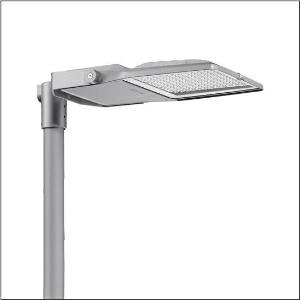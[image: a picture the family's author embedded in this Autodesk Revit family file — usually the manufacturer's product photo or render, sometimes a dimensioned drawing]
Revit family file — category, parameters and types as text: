
# Revit family: floodlight_fl_21_iq_midi___pl64_5xa7782f4e3a_0b41
name_source: partatom
category: Lighting Fixtures
units: mm (PartAtom-declared; Revit-internal decimal feet)

## family parameters
Cut with Voids When Loaded = No
Host = Face
Light Source = No
Part Type = Normal
Room Calculation Point = No
Round Connector Dimension = Use Diameter
Shared = No

## types (1)
- --- (1 x LED, 36050 lm, 270.2 W, 4000K)
    Apparent Load = 270 VA
    CIE Flux Codes = 28 80 98 100 100
    Color Rendering = 70
    Color Temperature = 4000K
    Default Elevation = 1800 mm
    Description = Floodlight FL 21 iQ midi, floodlight, primary light control with lens, of PMMA, primary optical cover: protective disc, of toughened safety glass, transparent, light distribution: PL64, light emission: direct distribution, installation type: surface-mounted, lamps: LED, High Power LED, rated values: 36.050lm | 270,2W | 133,4lm/W (begin service life); end service life: 36.050lm | 286,6W; at 50% lumin. flux: 18.025lm | 117,7W | 153,1lm/W, colour temperature: 4000K, colour rendering: CRI > 70, light colour: 740, light setting 1 begin service life: 100% | 36.050lm | 270,2W | 133,4lm/W | 4.000K, light setting 1 end service life: 286,6W, further light settings possible, control: optimised constant luminous flux control (CLO 2.0), Desk-Remote (wireless, voltage-free reading and setting of iQ features in the workshop via application-optimized NFC function/RFID function), Smart-Wire, Night-Set, Temp-Guard, Auto-Match, Street-Remote, pre-setting: linear dimming characteristic, with terminal, 6-pole, mains connection: 220..240V, AC, 50/60Hz, luminaire housing, of diecast aluminium, powder-coated, SITECO metallic grey (DB 702S), corrosivity category C5 mid according to DIN EN ISO 12944suitable for swimming poolschlorine-resistant, sealing non-destructively replaceable, please order mast flange separately, mast bracket, of steel, galvanised, powder-coated, SITECO metallic grey (DB 702S), protection rating (complete): IP66, insulation class (complete): insulation class II (safety insulation), certification: CE, ENEC, VDE, protection symbol: D, impact resistance: IK08, permissible operating ambient temperature: -40..+40°C, permissible operating ambient temperature for outdoor applications: -40..+50°C, standard: DIN EN 12944, LABS conformity tested according to VDMA 24364:2018-05, packaging unit: 1 piece

Light Distribution: PL64
    Height = 76 mm
    Lamp = 1 x LED
    Lamp Light Flux = 36050 lm
    Lamp Power = 270.2 W
    Lamp count = 1
    Length = 657 mm
    Luminous efficacy = 133 lm/W
    Manufacturer = Siteco
    ModVariant = No
    Model = 5XA7782F4E3A
    Mounting Place = Pole
    Mounting Type = Pole annexe
    Number of Poles = 1
    OnlyDefault = Yes
    Power Factor = 1
    Product Name = Floodlight FL 21 iQ midi | PL64
    Product group = floodlight | pylon annexe
    ProductGroupID = 6201
    Protection Class = Protection class II
    Protection Degree = IP 66
    RLX_Detail_Level = 1
    RLX_Emergency_Light_Flux = 0 lm
    RLX_Emergency_Type = 0
    RLX_Emergency_Type_DB = No
    RlxData = <blob elided: 153805 chars, md5=7e72a45a>
    Socket = socket
    Standby Power = 0 W
    System Light Flux = 36050 lm
    System Power = 270 W
    Type Comments = factory setting: luminous flux: 100 % | dim-lin: 254 | 620 mA
    Type Image = l_1007123.jpg
    URL = http://relux.com
    VarID = @adj_108065
    Voltage = 0 V
    Weight = 0.00 kg
    Width = 442 mm

## geometry (parser evidence)
native form markers: Blend x4, Sweep x11
no freeform markers — native parametric forms only
